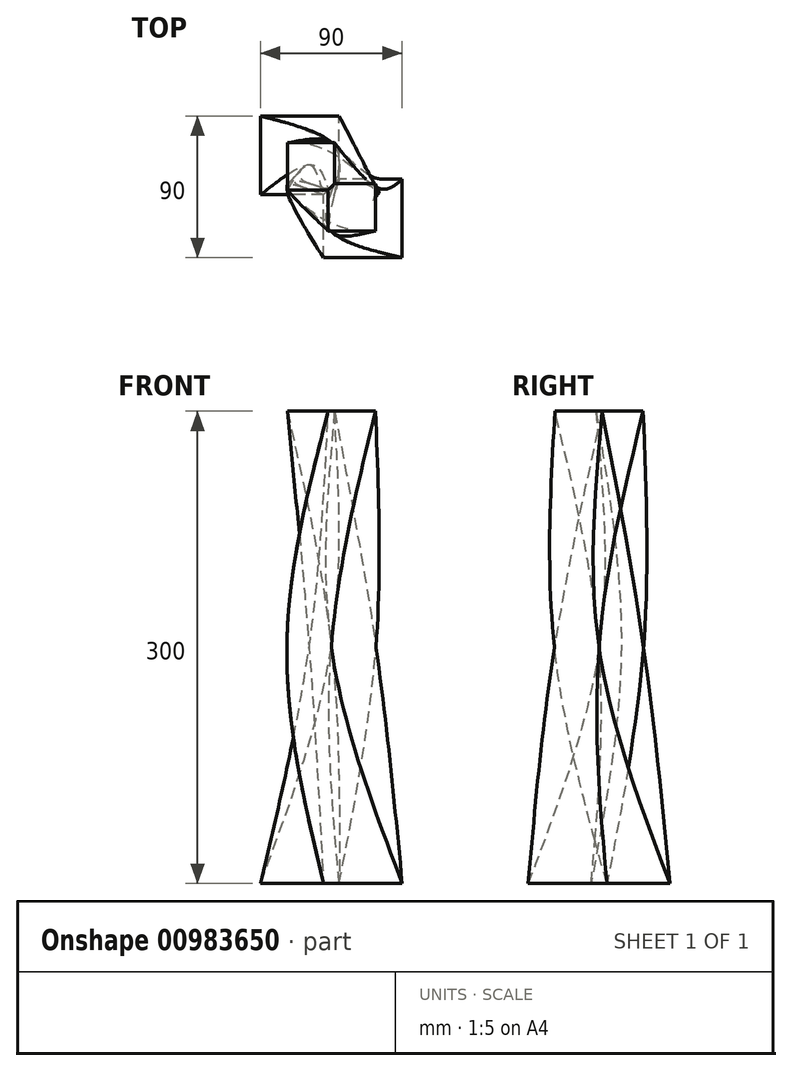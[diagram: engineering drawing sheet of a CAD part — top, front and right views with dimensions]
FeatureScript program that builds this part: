
annotation { "Feature Type Name" : "Feature", "Feature Type Description" : "" }
export const myFeature = defineFeature(function(context is Context, id is Id, definition is map)
    precondition{}
    {
        {
            var Q0;
            Q0=qCreatedBy(makeId("Top.planeOp"),FACE);
            var sketch = newSketch(context, id + "F0", { "sketchPlane" : qUnion([Q0])});
            skLineSegment(sketch, "E0.top", {"start": v(-5, -45) * mm, "end": v(45, -45) * mm});
            skLineSegment(sketch, "E0.right", {"start": v(45, 5) * mm, "end": v(45, -45) * mm});
            skLineSegment(sketch, "E1.bottom", {"start": v(-45, 45) * mm, "end": v(5, 45) * mm});
            skLineSegment(sketch, "E1.left", {"start": v(-45, 45) * mm, "end": v(-45, -5) * mm});
            skLineSegment(sketch, "E2", {"start": v(-20, 45) * mm, "end": v(-20, -5) * mm, "construction": true});
            skLineSegment(sketch, "E3", {"start": v(-45, 20) * mm, "end": v(5, 20) * mm, "construction": true});
            skLineSegment(sketch, "E4", {"start": v(20, 5) * mm, "end": v(20, -45) * mm, "construction": true});
            skLineSegment(sketch, "E5", {"start": v(-5, -20) * mm, "end": v(45, -20) * mm, "construction": true});
            skPoint(sketch, "E6", {"position": v(-20, 20) * mm});
            skPoint(sketch, "E7", {"position": v(20, -20) * mm});
            skLineSegment(sketch, "E8", {"start": v(45, 5) * mm, "end": v(5, 5) * mm});
            skLineSegment(sketch, "E9", {"start": v(5, 5) * mm, "end": v(5, 45) * mm});
            skLineSegment(sketch, "E10", {"start": v(-5, -45) * mm, "end": v(-5, -5) * mm});
            skLineSegment(sketch, "E11", {"start": v(-5, -5) * mm, "end": v(5, 5) * mm});
            skLineSegment(sketch, "E12", {"start": v(-5, -5) * mm, "end": v(-45, -5) * mm});
            skSolve(sketch);
        }
        {
            var Q0;
            Q0=qCreatedBy(makeId("Top.planeOp"),FACE);
            cPlane(context, id + "F1", {"entities" : qUnion([Q0]), "cplaneType" : CPlaneType.OFFSET, "offset" : 150 * mm, "width" : 150 * mm, "height" : 150 * mm});
        }
        {
            var Q0;
            Q0=qCreatedBy(id+"F1.planeOp",FACE);
            var sketch = newSketch(context, id + "F2", { "sketchPlane" : qUnion([Q0])});
            skLineSegment(sketch, "E13.bottom", {"start": v(0, 28.28) * mm, "end": v(28.28, 0) * mm});
            skLineSegment(sketch, "E13.top", {"start": v(-28.28, 0) * mm, "end": v(0, -28.28) * mm});
            skLineSegment(sketch, "E13.left", {"start": v(0, 28.28) * mm, "end": v(-28.28, 0) * mm});
            skLineSegment(sketch, "E13.right", {"start": v(28.28, 0) * mm, "end": v(0, -28.28) * mm});
            skLineSegment(sketch, "E14", {"start": v(14.14, 14.14) * mm, "end": v(-14.14, -14.14) * mm, "construction": true});
            skLineSegment(sketch, "E15", {"start": v(-14.14, 14.14) * mm, "end": v(14.14, -14.14) * mm, "construction": true});
            skPoint(sketch, "E16", {"position": v(0, 0) * mm});
            skSolve(sketch);
        }
        {
            var Q0;
            Q0=qCreatedBy(id+"F1.planeOp",FACE);
            cPlane(context, id + "F3", {"entities" : qUnion([Q0]), "cplaneType" : CPlaneType.OFFSET, "offset" : 150 * mm, "width" : 150 * mm, "height" : 150 * mm});
        }
        {
            var Q0;
            Q0=qCreatedBy(id+"F3.planeOp",FACE);
            var sketch = newSketch(context, id + "F4", { "sketchPlane" : qUnion([Q0])});
            skLineSegment(sketch, "E17.bottom", {"start": v(-28, 28) * mm, "end": v(2, 28) * mm});
            skLineSegment(sketch, "E17.left", {"start": v(-28, 28) * mm, "end": v(-28, -2) * mm});
            skLineSegment(sketch, "E18.top", {"start": v(-2, -28) * mm, "end": v(28, -28) * mm});
            skLineSegment(sketch, "E18.right", {"start": v(28, 2) * mm, "end": v(28, -28) * mm});
            skLineSegment(sketch, "E19", {"start": v(13, 2) * mm, "end": v(13, -28) * mm, "construction": true});
            skLineSegment(sketch, "E20", {"start": v(-2, -13) * mm, "end": v(28, -13) * mm, "construction": true});
            skLineSegment(sketch, "E21", {"start": v(-13, 28) * mm, "end": v(-13, -2) * mm, "construction": true});
            skLineSegment(sketch, "E22", {"start": v(-28, 13) * mm, "end": v(2, 13) * mm, "construction": true});
            skPoint(sketch, "E23", {"position": v(13, -13) * mm});
            skPoint(sketch, "E24", {"position": v(-13, 13) * mm});
            skLineSegment(sketch, "E25", {"start": v(-28, -2) * mm, "end": v(-2, -2) * mm});
            skLineSegment(sketch, "E26", {"start": v(2, 28) * mm, "end": v(2, 2) * mm});
            skLineSegment(sketch, "E27", {"start": v(28, 2) * mm, "end": v(2, 2) * mm});
            skLineSegment(sketch, "E28", {"start": v(-2, -2) * mm, "end": v(-2, -28) * mm});
            skLineSegment(sketch, "E29", {"start": v(2, 2) * mm, "end": v(-2, -2) * mm});
            skSolve(sketch);
        }
        {
            var Q0;
            Q0=makeQuery(id+"F4.imprint","IMPRINT",FACE,{"disambiguationData":[TD([[makeQuery(id+"F4.imprint","IMPRINT",EDGE,{"derivedFrom":sQuery(id+"F4.wireOp",EDGE,"E17.bottom")}),-1.0]])]});
            var Q1;
            Q1=makeQuery(id+"F2.imprint","IMPRINT",FACE,{"disambiguationData":[TD([[makeQuery(id+"F2.imprint","IMPRINT",EDGE,{"derivedFrom":sQuery(id+"F2.wireOp",EDGE,"E13.bottom")}),-1.0]])]});
            var Q2;
            Q2=makeQuery(id+"F0.imprint","IMPRINT",FACE,{"disambiguationData":[TD([[makeQuery(id+"F0.imprint","IMPRINT",EDGE,{"derivedFrom":sQuery(id+"F0.wireOp",EDGE,"E0.top")}),1.0]])]});
            loft(context, id + "F5", {"sheetProfilesArray" : [{ "sheetProfileEntities" : qUnion([Q0]) }, { "sheetProfileEntities" : qUnion([Q1]) }, { "sheetProfileEntities" : qUnion([Q2]) }]});
        }
        {
            var Q0;
            Q0=makeQuery(id+"F0.imprint","IMPRINT",FACE,{"disambiguationData":[TD([[makeQuery(id+"F0.imprint","IMPRINT",EDGE,{"derivedFrom":sQuery(id+"F0.wireOp",EDGE,"E1.bottom")}),-1.0]])]});
            var Q1;
            Q1=makeQuery(id+"F2.imprint","IMPRINT",FACE,{"disambiguationData":[TD([[makeQuery(id+"F2.imprint","IMPRINT",EDGE,{"derivedFrom":sQuery(id+"F2.wireOp",EDGE,"E13.bottom")}),-1.0]])]});
            var Q2;
            Q2=makeQuery(id+"F4.imprint","IMPRINT",FACE,{"disambiguationData":[TD([[makeQuery(id+"F4.imprint","IMPRINT",EDGE,{"derivedFrom":sQuery(id+"F4.wireOp",EDGE,"E18.top")}),1.0]])]});
            var Q3;
            Q3=makeQuery(id+"F0.imprint","IMPRINT",FACE,{"disambiguationData":[TD([[makeQuery(id+"F0.imprint","IMPRINT",EDGE,{"derivedFrom":sQuery(id+"F0.wireOp",EDGE,"E1.bottom")}),-1.0]])]});
            var Q4;
            Q4=makeQuery(id+"F2.imprint","IMPRINT",FACE,{"disambiguationData":[TD([[makeQuery(id+"F2.imprint","IMPRINT",EDGE,{"derivedFrom":sQuery(id+"F2.wireOp",EDGE,"E13.bottom")}),-1.0]])]});
            var Q5;
            Q5=makeQuery(id+"F4.imprint","IMPRINT",FACE,{"disambiguationData":[TD([[makeQuery(id+"F4.imprint","IMPRINT",EDGE,{"derivedFrom":sQuery(id+"F4.wireOp",EDGE,"E18.top")}),1.0]])]});
            loft(context, id + "F6", {"sheetProfilesArray" : [{ "sheetProfileEntities" : qUnion([Q0]) }, { "sheetProfileEntities" : qUnion([Q1]) }, { "sheetProfileEntities" : qUnion([Q2]) }], "wireProfilesArray" : [{ "wireProfileEntities" : qUnion([Q3]) }, { "wireProfileEntities" : qUnion([Q4]) }, { "wireProfileEntities" : qUnion([Q5]) }]});
        }
    });
